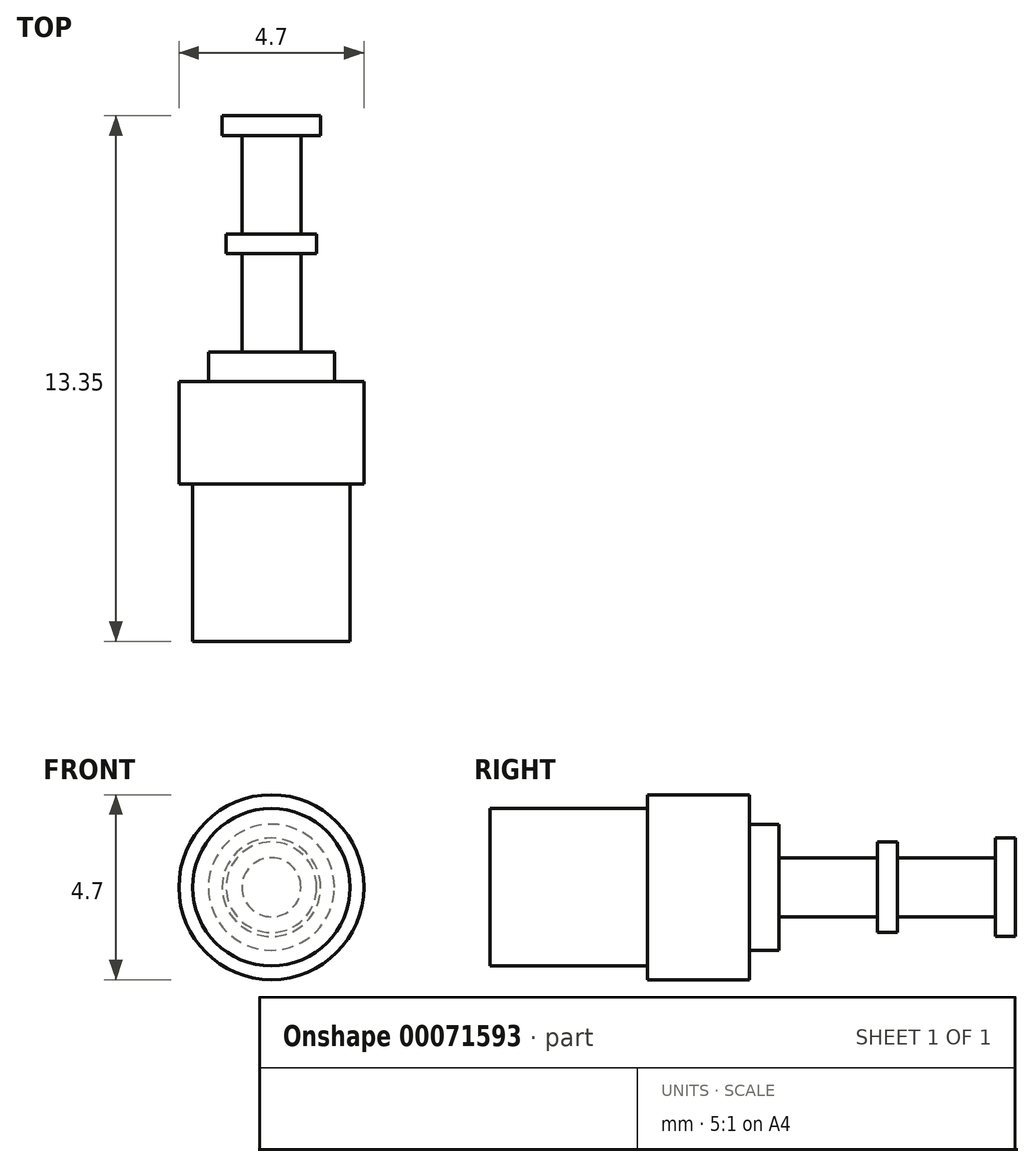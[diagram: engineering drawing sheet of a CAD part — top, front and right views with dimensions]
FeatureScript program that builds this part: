
annotation { "Feature Type Name" : "Feature", "Feature Type Description" : "" }
export const myFeature = defineFeature(function(context is Context, id is Id, definition is map)
    precondition{}
    {
        {
            var Q0;
            Q0=qCreatedBy(makeId("Front.planeOp"),FACE);
            var sketch = newSketch(context, id + "F0", { "sketchPlane" : qUnion([Q0])});
            skCircle(sketch, "E0", {"center": v(0, 0) * mm, "radius": 2.35 * mm});
            skSolve(sketch);
        }
        {
            var Q0;
            Q0 = qSketchRegion(id + "F0", true);
            extrude(context, id + "F1", {"entities" : qUnion([Q0]), "depth" : 2.6 * mm});
        }
        {
            var Q0;
            Q0=makeQuery(id+"F1.opExtrude","CAP_FACE",FACE,{"disambiguationData":[OSD([sQuery(id+"F0.wireOp",EDGE,"E0")])],"isStart":false});
            var sketch = newSketch(context, id + "F2", { "sketchPlane" : qUnion([Q0])});
            skCircle(sketch, "E1", {"center": v(0, 0) * mm, "radius": 2 * mm});
            skSolve(sketch);
        }
        {
            var Q0;
            Q0 = qSketchRegion(id + "F2", true);
            extrude(context, id + "F3", {"entities" : qUnion([Q0]), "operationType" : NewBodyOperationType.ADD, "depth" : 4 * mm});
        }
        {
            var Q0;
            Q0=makeQuery(id+"F1.opExtrude","CAP_FACE",FACE,{"disambiguationData":[OSD([sQuery(id+"F0.wireOp",EDGE,"E0")])],"isStart":true});
            var sketch = newSketch(context, id + "F4", { "sketchPlane" : qUnion([Q0])});
            skCircle(sketch, "E2", {"center": v(0, 0) * mm, "radius": 1.6 * mm});
            skSolve(sketch);
        }
        {
            var Q0;
            Q0 = qSketchRegion(id + "F4", true);
            extrude(context, id + "F5", {"entities" : qUnion([Q0]), "depth" : 0.75 * mm});
        }
        {
            var Q0;
            Q0=makeQuery(id+"F5.opExtrude","CAP_FACE",FACE,{"disambiguationData":[OSD([sQuery(id+"F4.wireOp",EDGE,"E2")])],"isStart":false});
            var sketch = newSketch(context, id + "F6", { "sketchPlane" : qUnion([Q0])});
            skCircle(sketch, "E3", {"center": v(0, 0) * mm, "radius": 0.75 * mm});
            skSolve(sketch);
        }
        {
            var Q0;
            Q0 = qSketchRegion(id + "F6", true);
            extrude(context, id + "F7", {"entities" : qUnion([Q0]), "operationType" : NewBodyOperationType.ADD, "depth" : 2.5 * mm});
        }
        {
            var Q0;
            Q0=makeQuery(id+"F7.opExtrude","CAP_FACE",FACE,{"disambiguationData":[OSD([sQuery(id+"F6.wireOp",EDGE,"E3")])],"isStart":false});
            var sketch = newSketch(context, id + "F8", { "sketchPlane" : qUnion([Q0])});
            skCircle(sketch, "E4", {"center": v(0, 0) * mm, "radius": 1.15 * mm});
            skSolve(sketch);
        }
        {
            var Q0;
            Q0 = qSketchRegion(id + "F8", true);
            extrude(context, id + "F9", {"entities" : qUnion([Q0]), "operationType" : NewBodyOperationType.ADD, "depth" : 0.5 * mm});
        }
        {
            var Q0;
            Q0=makeQuery(id+"F9.opExtrude","CAP_FACE",FACE,{"disambiguationData":[OSD([sQuery(id+"F8.wireOp",EDGE,"E4")])],"isStart":false});
            var sketch = newSketch(context, id + "F10", { "sketchPlane" : qUnion([Q0])});
            skCircle(sketch, "E5", {"center": v(0, 0) * mm, "radius": 0.75 * mm});
            skSolve(sketch);
        }
        {
            var Q0;
            Q0 = qSketchRegion(id + "F10", true);
            extrude(context, id + "F11", {"entities" : qUnion([Q0]), "operationType" : NewBodyOperationType.ADD, "depth" : 2.5 * mm});
        }
        {
            var Q0;
            Q0=makeQuery(id+"F11.opExtrude","CAP_FACE",FACE,{"disambiguationData":[OSD([sQuery(id+"F10.wireOp",EDGE,"E5")])],"isStart":false});
            var sketch = newSketch(context, id + "F12", { "sketchPlane" : qUnion([Q0])});
            skCircle(sketch, "E6", {"center": v(0, 0) * mm, "radius": 1.25 * mm});
            skSolve(sketch);
        }
        {
            var Q0;
            Q0 = qSketchRegion(id + "F12", true);
            extrude(context, id + "F13", {"entities" : qUnion([Q0]), "operationType" : NewBodyOperationType.ADD, "depth" : 0.5 * mm});
        }
    });
